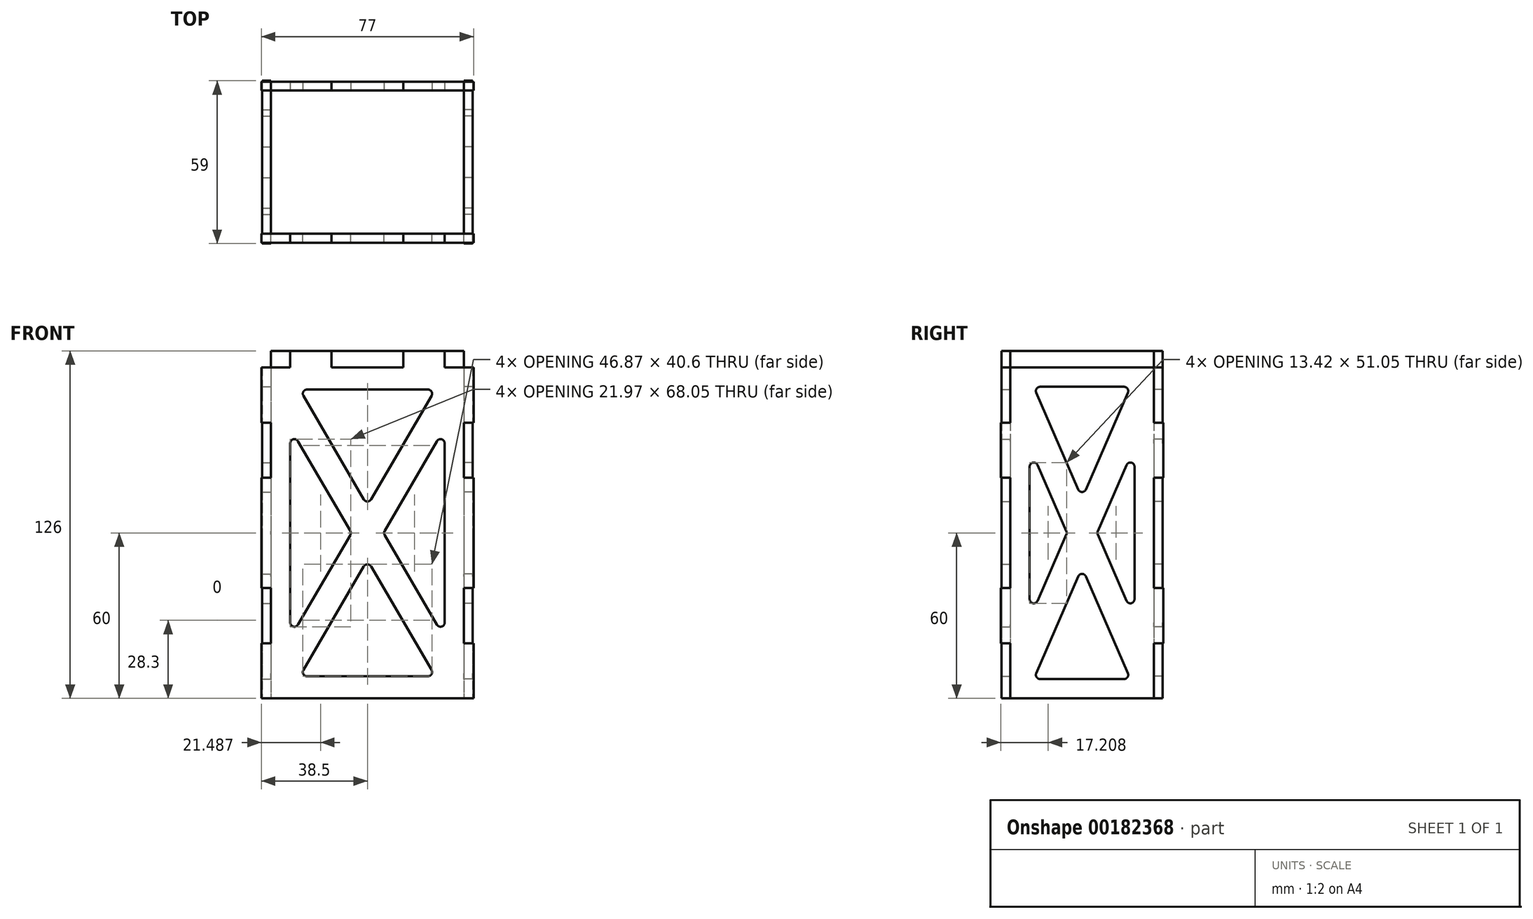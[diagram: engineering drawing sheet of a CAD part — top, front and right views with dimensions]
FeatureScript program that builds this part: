
annotation { "Feature Type Name" : "Feature", "Feature Type Description" : "" }
export const myFeature = defineFeature(function(context is Context, id is Id, definition is map)
    precondition{}
    {
        {
            var Q0;
            Q0=qCreatedBy(makeId("Top.planeOp"),FACE);
            var sketch = newSketch(context, id + "F0", { "sketchPlane" : qUnion([Q0])});
            skLineSegment(sketch, "E0.bottom", {"start": v(35, -26) * mm, "end": v(-35, -26) * mm});
            skLineSegment(sketch, "E0.top", {"start": v(35, 26) * mm, "end": v(-35, 26) * mm});
            skLineSegment(sketch, "E0.left", {"start": v(35, -26) * mm, "end": v(35, 26) * mm});
            skLineSegment(sketch, "E0.right", {"start": v(-35, -26) * mm, "end": v(-35, 26) * mm});
            skPoint(sketch, "E0.middle", {"position": v(0, 0) * mm});
            skSolve(sketch);
        }
        {
            var Q0;
            Q0 = qSketchRegion(id + "F0", true);
            extrude(context, id + "F1", {"entities" : qUnion([Q0]), "depth" : 126 * mm, "offsetDistance" : 25 * mm});
        }
        {
            var Q0;
            Q0=makeQuery(id+"F1.opExtrude","SWEPT_FACE",FACE,{"disambiguationData":[OSD([sQuery(id+"F0.wireOp",EDGE,"E0.bottom")])]});
            var sketch = newSketch(context, id + "F2", { "sketchPlane" : qUnion([Q0])});
            skLineSegment(sketch, "E1.0", {"start": v(28, 126) * mm, "end": v(13, 126) * mm});
            skLineSegment(sketch, "E2.0", {"start": v(38.5, 0) * mm, "end": v(-38.5, 0) * mm});
            skLineSegment(sketch, "E3.0", {"start": v(-38.5, 120) * mm, "end": v(-38.5, 100) * mm});
            skLineSegment(sketch, "E4.0", {"start": v(38.5, 120) * mm, "end": v(38.5, 100) * mm});
            skLineSegment(sketch, "E5.0", {"start": v(38.5, 120) * mm, "end": v(28, 120) * mm});
            skLineSegment(sketch, "E6.0", {"start": v(38.5, 100) * mm, "end": v(35, 100) * mm});
            skLineSegment(sketch, "E7.0", {"start": v(38.5, 80) * mm, "end": v(35, 80) * mm});
            skLineSegment(sketch, "E8.0", {"start": v(38.5, 20) * mm, "end": v(35, 20) * mm});
            skLineSegment(sketch, "E9.0", {"start": v(38.5, 40) * mm, "end": v(35, 40) * mm});
            skLineSegment(sketch, "E10.trimOffspring", {"start": v(-38.5, 80) * mm, "end": v(-38.5, 40) * mm});
            skLineSegment(sketch, "E11.trimOffspring", {"start": v(38.5, 80) * mm, "end": v(38.5, 40) * mm});
            skLineSegment(sketch, "E12.trimOffspring", {"start": v(35, 100) * mm, "end": v(35, 80) * mm});
            skLineSegment(sketch, "E13.trimOffspring", {"start": v(-28, 120) * mm, "end": v(-38.5, 120) * mm});
            skLineSegment(sketch, "E14.trimOffspring", {"start": v(-35, 100) * mm, "end": v(-35, 80) * mm});
            skLineSegment(sketch, "E15.trimOffspring", {"start": v(-35, 40) * mm, "end": v(-35, 20) * mm});
            skLineSegment(sketch, "E16.trimOffspring", {"start": v(38.5, 20) * mm, "end": v(38.5, 0) * mm});
            skLineSegment(sketch, "E17.trimOffspring", {"start": v(-38.5, 20) * mm, "end": v(-38.5, 0) * mm});
            skLineSegment(sketch, "E18.trimOffspring", {"start": v(35, 40) * mm, "end": v(35, 20) * mm});
            skLineSegment(sketch, "E19.trimOffspring", {"start": v(-35, 20) * mm, "end": v(-38.5, 20) * mm});
            skLineSegment(sketch, "E20.trimOffspring", {"start": v(-35, 40) * mm, "end": v(-38.5, 40) * mm});
            skLineSegment(sketch, "E21.trimOffspring", {"start": v(-35, 80) * mm, "end": v(-38.5, 80) * mm});
            skLineSegment(sketch, "E22.trimOffspring", {"start": v(-35, 100) * mm, "end": v(-38.5, 100) * mm});
            skPoint(sketch, "E23", {"position": v(0, 126) * mm});
            skLineSegment(sketch, "E24", {"start": v(-13, 126) * mm, "end": v(-13, 120) * mm});
            skLineSegment(sketch, "E25", {"start": v(-28, 126) * mm, "end": v(-28, 120) * mm});
            skLineSegment(sketch, "E26", {"start": v(13, 126) * mm, "end": v(13, 120) * mm});
            skLineSegment(sketch, "E27", {"start": v(28, 126) * mm, "end": v(28, 120) * mm});
            skPoint(sketch, "E28.0.start.orphan", {"position": v(-35, 126) * mm});
            skLineSegment(sketch, "E29.trimOffspring", {"start": v(-13, 126) * mm, "end": v(-28, 126) * mm});
            skPoint(sketch, "E30.0.start.orphan", {"position": v(35, 126) * mm});
            skLineSegment(sketch, "E31", {"start": v(-13, 120) * mm, "end": v(13, 120) * mm});
            skLineSegment(sketch, "E32", {"start": v(-35, 120) * mm, "end": v(35, 0) * mm, "construction": true});
            skLineSegment(sketch, "E33", {"start": v(35, 120) * mm, "end": v(-35, 0) * mm, "construction": true});
            skLineSegment(sketch, "E34", {"start": v(-28, 92.53) * mm, "end": v(-28, 27.47) * mm});
            skLineSegment(sketch, "E35", {"start": v(28, 92.53) * mm, "end": v(28, 27.47) * mm});
            skLineSegment(sketch, "E36", {"start": v(-21.93, 112) * mm, "end": v(21.93, 112) * mm});
            skLineSegment(sketch, "E37", {"start": v(-21.93, 8) * mm, "end": v(21.93, 8) * mm});
            skLineSegment(sketch, "E38.trimOffspring", {"start": v(-25.2, 93.28) * mm, "end": v(-6.23, 60.76) * mm});
            skLineSegment(sketch, "E39.trimOffspring", {"start": v(-23.23, 109.74) * mm, "end": v(-1.3, 72.14) * mm});
            skLineSegment(sketch, "E40.trimOffspring", {"start": v(25.2, 93.28) * mm, "end": v(6.23, 60.76) * mm});
            skLineSegment(sketch, "E41.trimOffspring", {"start": v(23.23, 109.74) * mm, "end": v(1.3, 72.14) * mm});
            skLineSegment(sketch, "E42.trimOffspring", {"start": v(6.23, 59.24) * mm, "end": v(25.2, 26.72) * mm});
            skLineSegment(sketch, "E43.trimOffspring", {"start": v(-6.23, 59.24) * mm, "end": v(-25.2, 26.72) * mm});
            skLineSegment(sketch, "E44.trimOffspring", {"start": v(-1.3, 47.86) * mm, "end": v(-23.23, 10.26) * mm});
            skLineSegment(sketch, "E45.trimOffspring", {"start": v(1.3, 47.86) * mm, "end": v(23.23, 10.26) * mm});
            skPoint(sketch, "E46.visualSharp", {"position": v(-28, 98.08) * mm});
            skArc(sketch, "E46.filletArc", {"start": v(-25.2, 93.28) * mm, "mid": v(-26.9, 93.98) * mm, "end": v(-28, 92.53) * mm});
            skPoint(sketch, "E47.visualSharp", {"position": v(-5.79, 60) * mm});
            skArc(sketch, "E47.filletArc", {"start": v(-6.23, 59.24) * mm, "mid": v(-6.03, 60) * mm, "end": v(-6.23, 60.76) * mm});
            skPoint(sketch, "E48.visualSharp", {"position": v(-28, 21.92) * mm});
            skArc(sketch, "E48.filletArc", {"start": v(-28, 27.47) * mm, "mid": v(-26.9, 26.02) * mm, "end": v(-25.2, 26.72) * mm});
            skPoint(sketch, "E49.visualSharp", {"position": v(-24.54, 8) * mm});
            skArc(sketch, "E49.filletArc", {"start": v(-23.23, 10.26) * mm, "mid": v(-23.23, 8.75) * mm, "end": v(-21.93, 8) * mm});
            skPoint(sketch, "E50.visualSharp", {"position": v(0, 50.08) * mm});
            skArc(sketch, "E50.filletArc", {"start": v(1.3, 47.86) * mm, "mid": v(0, 48.6) * mm, "end": v(-1.3, 47.86) * mm});
            skPoint(sketch, "E51.visualSharp", {"position": v(24.54, 8) * mm});
            skArc(sketch, "E51.filletArc", {"start": v(21.93, 8) * mm, "mid": v(23.23, 8.75) * mm, "end": v(23.23, 10.26) * mm});
            skPoint(sketch, "E52.visualSharp", {"position": v(5.79, 60) * mm});
            skArc(sketch, "E52.filletArc", {"start": v(6.23, 60.76) * mm, "mid": v(6.03, 60) * mm, "end": v(6.23, 59.24) * mm});
            skPoint(sketch, "E53.visualSharp", {"position": v(28, 21.92) * mm});
            skArc(sketch, "E53.filletArc", {"start": v(25.2, 26.72) * mm, "mid": v(26.9, 26.02) * mm, "end": v(28, 27.47) * mm});
            skPoint(sketch, "E54.visualSharp", {"position": v(28, 98.08) * mm});
            skArc(sketch, "E54.filletArc", {"start": v(28, 92.53) * mm, "mid": v(26.9, 93.98) * mm, "end": v(25.2, 93.28) * mm});
            skPoint(sketch, "E55.visualSharp", {"position": v(24.54, 112) * mm});
            skArc(sketch, "E55.filletArc", {"start": v(23.23, 109.74) * mm, "mid": v(23.23, 111.25) * mm, "end": v(21.93, 112) * mm});
            skPoint(sketch, "E56.visualSharp", {"position": v(-24.54, 112) * mm});
            skArc(sketch, "E56.filletArc", {"start": v(-21.93, 112) * mm, "mid": v(-23.23, 111.25) * mm, "end": v(-23.23, 109.74) * mm});
            skPoint(sketch, "E57.visualSharp", {"position": v(0, 69.92) * mm});
            skArc(sketch, "E57.filletArc", {"start": v(-1.3, 72.14) * mm, "mid": v(0, 71.4) * mm, "end": v(1.3, 72.14) * mm});
            skSolve(sketch);
        }
        {
            var Q0;
            Q0 = qSketchRegion(id + "F2", true);
            extrude(context, id + "F3", {"entities" : qUnion([Q0]), "depth" : 3.2 * mm, "offsetDistance" : 25 * mm});
        }
        {
            var Q0;
            Q0=makeQuery(id+"F1.opExtrude","SWEPT_FACE",FACE,{"disambiguationData":[OSD([sQuery(id+"F0.wireOp",EDGE,"E0.top")])]});
            var sketch = newSketch(context, id + "F4", { "sketchPlane" : qUnion([Q0])});
            skLineSegment(sketch, "E58.0.0", {"start": v(-38.5, 0) * mm, "end": v(-38.5, 20) * mm});
            skLineSegment(sketch, "E58.0.1", {"start": v(-38.5, 20) * mm, "end": v(-35, 20) * mm});
            skLineSegment(sketch, "E58.0.2", {"start": v(-35, 20) * mm, "end": v(-35, 40) * mm});
            skLineSegment(sketch, "E58.0.3", {"start": v(-35, 40) * mm, "end": v(-38.5, 40) * mm});
            skLineSegment(sketch, "E58.0.4", {"start": v(-38.5, 40) * mm, "end": v(-38.5, 80) * mm});
            skLineSegment(sketch, "E58.0.5", {"start": v(-38.5, 80) * mm, "end": v(-35, 80) * mm});
            skLineSegment(sketch, "E58.0.6", {"start": v(-35, 80) * mm, "end": v(-35, 100) * mm});
            skLineSegment(sketch, "E58.0.7", {"start": v(-35, 100) * mm, "end": v(-38.5, 100) * mm});
            skLineSegment(sketch, "E58.0.8", {"start": v(-38.5, 100) * mm, "end": v(-38.5, 120) * mm});
            skLineSegment(sketch, "E58.0.9", {"start": v(-38.5, 120) * mm, "end": v(-35, 120) * mm});
            skLineSegment(sketch, "E58.0.11", {"start": v(-35, 126) * mm, "end": v(-13, 126) * mm});
            skLineSegment(sketch, "E58.0.12", {"start": v(-13, 126) * mm, "end": v(-13, 120) * mm});
            skLineSegment(sketch, "E58.0.13", {"start": v(-13, 120) * mm, "end": v(13, 120) * mm});
            skLineSegment(sketch, "E58.0.14", {"start": v(13, 120) * mm, "end": v(13, 126) * mm});
            skLineSegment(sketch, "E58.0.15", {"start": v(13, 126) * mm, "end": v(35, 126) * mm});
            skLineSegment(sketch, "E58.0.17", {"start": v(35, 120) * mm, "end": v(38.5, 120) * mm});
            skLineSegment(sketch, "E58.0.18", {"start": v(38.5, 120) * mm, "end": v(38.5, 100) * mm});
            skLineSegment(sketch, "E58.0.19", {"start": v(38.5, 100) * mm, "end": v(35, 100) * mm});
            skLineSegment(sketch, "E58.0.20", {"start": v(35, 100) * mm, "end": v(35, 80) * mm});
            skLineSegment(sketch, "E58.0.21", {"start": v(35, 80) * mm, "end": v(38.5, 80) * mm});
            skLineSegment(sketch, "E58.0.22", {"start": v(38.5, 80) * mm, "end": v(38.5, 40) * mm});
            skLineSegment(sketch, "E58.0.23", {"start": v(38.5, 40) * mm, "end": v(35, 40) * mm});
            skLineSegment(sketch, "E58.0.24", {"start": v(35, 40) * mm, "end": v(35, 20) * mm});
            skLineSegment(sketch, "E58.0.25", {"start": v(35, 20) * mm, "end": v(38.5, 20) * mm});
            skLineSegment(sketch, "E58.0.26", {"start": v(38.5, 20) * mm, "end": v(38.5, 0) * mm});
            skLineSegment(sketch, "E58.0.27", {"start": v(38.5, 0) * mm, "end": v(-38.5, 0) * mm});
            skLineSegment(sketch, "E59.0", {"start": v(-23.23, 109.74) * mm, "end": v(-1.3, 72.14) * mm});
            skArc(sketch, "E60.0", {"start": v(-23.23, 109.74) * mm, "mid": v(-23.23, 111.25) * mm, "end": v(-21.93, 112) * mm});
            skLineSegment(sketch, "E61.0", {"start": v(21.93, 112) * mm, "end": v(-21.93, 112) * mm});
            skLineSegment(sketch, "E62.0", {"start": v(23.23, 109.74) * mm, "end": v(1.3, 72.14) * mm});
            skArc(sketch, "E63.0", {"start": v(21.93, 112) * mm, "mid": v(23.23, 111.25) * mm, "end": v(23.23, 109.74) * mm});
            skArc(sketch, "E64.0", {"start": v(1.3, 72.14) * mm, "mid": v(0, 71.4) * mm, "end": v(-1.3, 72.14) * mm});
            skLineSegment(sketch, "E65.0", {"start": v(-25.2, 93.28) * mm, "end": v(-6.23, 60.76) * mm});
            skArc(sketch, "E66.0", {"start": v(-28, 92.53) * mm, "mid": v(-26.9, 93.98) * mm, "end": v(-25.2, 93.28) * mm});
            skLineSegment(sketch, "E67.0", {"start": v(-28, 92.53) * mm, "end": v(-28, 27.47) * mm});
            skLineSegment(sketch, "E68.0", {"start": v(-6.23, 59.24) * mm, "end": v(-25.2, 26.72) * mm});
            skArc(sketch, "E69.0", {"start": v(-25.2, 26.72) * mm, "mid": v(-26.9, 26.02) * mm, "end": v(-28, 27.47) * mm});
            skArc(sketch, "E70.0", {"start": v(-6.23, 60.76) * mm, "mid": v(-6.03, 60) * mm, "end": v(-6.23, 59.24) * mm});
            skArc(sketch, "E71.0", {"start": v(6.23, 59.24) * mm, "mid": v(6.03, 60) * mm, "end": v(6.23, 60.76) * mm});
            skLineSegment(sketch, "E72.0", {"start": v(25.2, 93.28) * mm, "end": v(6.23, 60.76) * mm});
            skLineSegment(sketch, "E73.0", {"start": v(6.23, 59.24) * mm, "end": v(25.2, 26.72) * mm});
            skArc(sketch, "E74.0", {"start": v(25.2, 93.28) * mm, "mid": v(26.9, 93.98) * mm, "end": v(28, 92.53) * mm});
            skLineSegment(sketch, "E75.0", {"start": v(28, 92.53) * mm, "end": v(28, 27.47) * mm});
            skArc(sketch, "E76.0", {"start": v(28, 27.47) * mm, "mid": v(26.9, 26.02) * mm, "end": v(25.2, 26.72) * mm});
            skArc(sketch, "E77.0", {"start": v(-1.3, 47.86) * mm, "mid": v(0, 48.6) * mm, "end": v(1.3, 47.86) * mm});
            skLineSegment(sketch, "E78.0", {"start": v(1.3, 47.86) * mm, "end": v(23.23, 10.26) * mm});
            skLineSegment(sketch, "E79.0", {"start": v(-1.3, 47.86) * mm, "end": v(-23.23, 10.26) * mm});
            skArc(sketch, "E80.0", {"start": v(-21.93, 8) * mm, "mid": v(-23.23, 8.75) * mm, "end": v(-23.23, 10.26) * mm});
            skArc(sketch, "E81.0", {"start": v(23.23, 10.26) * mm, "mid": v(23.23, 8.75) * mm, "end": v(21.93, 8) * mm});
            skLineSegment(sketch, "E82.0", {"start": v(21.93, 8) * mm, "end": v(-21.93, 8) * mm});
            skLineSegment(sketch, "E83", {"start": v(-35, 120) * mm, "end": v(-35, 126) * mm});
            skLineSegment(sketch, "E84", {"start": v(35, 120) * mm, "end": v(35, 126) * mm});
            skPoint(sketch, "E85.orphan", {"position": v(28, 120) * mm});
            skPoint(sketch, "E86.orphan", {"position": v(-28, 120) * mm});
            skSolve(sketch);
        }
        {
            var Q0;
            Q0 = qSketchRegion(id + "F4", true);
            extrude(context, id + "F5", {"entities" : qUnion([Q0]), "depth" : 3.2 * mm, "offsetDistance" : 25 * mm});
        }
        {
            var Q0;
            Q0=makeQuery(id+"F1.opExtrude","SWEPT_FACE",FACE,{"disambiguationData":[OSD([sQuery(id+"F0.wireOp",EDGE,"E0.left")])]});
            var sketch = newSketch(context, id + "F6", { "sketchPlane" : qUnion([Q0])});
            skLineSegment(sketch, "E87.0", {"start": v(-26, 120) * mm, "end": v(-26, 100) * mm});
            skLineSegment(sketch, "E88.0", {"start": v(-29.5, 100) * mm, "end": v(-26, 100) * mm});
            skLineSegment(sketch, "E89.0", {"start": v(-29.5, 80) * mm, "end": v(-26, 80) * mm});
            skLineSegment(sketch, "E90.0", {"start": v(-26, 80) * mm, "end": v(-26, 40) * mm});
            skLineSegment(sketch, "E91.0", {"start": v(-29.5, 40) * mm, "end": v(-26, 40) * mm});
            skLineSegment(sketch, "E92.0", {"start": v(-29.5, 20) * mm, "end": v(-26, 20) * mm});
            skLineSegment(sketch, "E92.1", {"start": v(-26, 20) * mm, "end": v(-26, 0) * mm});
            skLineSegment(sketch, "E93.0", {"start": v(-26, 0) * mm, "end": v(26, 0) * mm});
            skLineSegment(sketch, "E94.0", {"start": v(26, 0) * mm, "end": v(26, 20) * mm});
            skLineSegment(sketch, "E95.0", {"start": v(29.5, 20) * mm, "end": v(26, 20) * mm});
            skLineSegment(sketch, "E96.0", {"start": v(29.5, 40) * mm, "end": v(26, 40) * mm});
            skLineSegment(sketch, "E97.0", {"start": v(26, 40) * mm, "end": v(26, 80) * mm});
            skLineSegment(sketch, "E98.0", {"start": v(29.5, 80) * mm, "end": v(26, 80) * mm});
            skLineSegment(sketch, "E99.0", {"start": v(29.5, 100) * mm, "end": v(26, 100) * mm});
            skLineSegment(sketch, "E100.0", {"start": v(26, 100) * mm, "end": v(26, 120) * mm});
            skLineSegment(sketch, "E101", {"start": v(-26, 120) * mm, "end": v(26, 120) * mm});
            skLineSegment(sketch, "E102.0", {"start": v(-26, 126) * mm, "end": v(-26, 0) * mm, "construction": true});
            skLineSegment(sketch, "E103.0", {"start": v(26, 126) * mm, "end": v(26, 0) * mm, "construction": true});
            skLineSegment(sketch, "E104.0", {"start": v(-29.5, 100) * mm, "end": v(-29.5, 80) * mm});
            skLineSegment(sketch, "E105.0", {"start": v(29.5, 100) * mm, "end": v(29.5, 80) * mm});
            skLineSegment(sketch, "E106.trimOffspring", {"start": v(29.5, 40) * mm, "end": v(29.5, 20) * mm});
            skLineSegment(sketch, "E107.trimOffspring", {"start": v(-29.5, 40) * mm, "end": v(-29.5, 20) * mm});
            skLineSegment(sketch, "E108", {"start": v(-26, 120) * mm, "end": v(26, 0) * mm, "construction": true});
            skLineSegment(sketch, "E109", {"start": v(26, 120) * mm, "end": v(-26, 0) * mm, "construction": true});
            skLineSegment(sketch, "E110", {"start": v(-15.23, 113) * mm, "end": v(15.23, 113) * mm});
            skLineSegment(sketch, "E111", {"start": v(-19, 84.04) * mm, "end": v(-19, 35.96) * mm});
            skLineSegment(sketch, "E112", {"start": v(19, 84.04) * mm, "end": v(19, 35.96) * mm});
            skLineSegment(sketch, "E113", {"start": v(-15.23, 7) * mm, "end": v(15.23, 7) * mm});
            skLineSegment(sketch, "E114.trimOffspring", {"start": v(5.7, 59.4) * mm, "end": v(16.12, 35.37) * mm});
            skLineSegment(sketch, "E115.trimOffspring", {"start": v(1.38, 44.25) * mm, "end": v(16.6, 9.1) * mm});
            skLineSegment(sketch, "E116.trimOffspring", {"start": v(-1.38, 44.25) * mm, "end": v(-16.6, 9.1) * mm});
            skLineSegment(sketch, "E117.trimOffspring", {"start": v(-5.7, 59.4) * mm, "end": v(-16.12, 35.37) * mm});
            skLineSegment(sketch, "E118.trimOffspring", {"start": v(-16.6, 110.9) * mm, "end": v(-1.38, 75.75) * mm});
            skLineSegment(sketch, "E119.trimOffspring", {"start": v(-16.12, 84.63) * mm, "end": v(-5.7, 60.6) * mm});
            skLineSegment(sketch, "E120.trimOffspring", {"start": v(16.6, 110.9) * mm, "end": v(1.38, 75.75) * mm});
            skLineSegment(sketch, "E121.trimOffspring", {"start": v(16.12, 84.63) * mm, "end": v(5.7, 60.6) * mm});
            skPoint(sketch, "E122.visualSharp", {"position": v(-17.52, 113) * mm});
            skArc(sketch, "E122.filletArc", {"start": v(-15.23, 113) * mm, "mid": v(-16.49, 112.32) * mm, "end": v(-16.6, 110.9) * mm});
            skPoint(sketch, "E123.visualSharp", {"position": v(17.52, 113) * mm});
            skArc(sketch, "E123.filletArc", {"start": v(16.6, 110.9) * mm, "mid": v(16.49, 112.32) * mm, "end": v(15.23, 113) * mm});
            skPoint(sketch, "E124.visualSharp", {"position": v(0, 72.58) * mm});
            skArc(sketch, "E124.filletArc", {"start": v(-1.38, 75.75) * mm, "mid": v(0, 74.85) * mm, "end": v(1.38, 75.75) * mm});
            skPoint(sketch, "E125.visualSharp", {"position": v(-19, 91.27) * mm});
            skArc(sketch, "E125.filletArc", {"start": v(-16.12, 84.63) * mm, "mid": v(-17.8, 85.5) * mm, "end": v(-19, 84.04) * mm});
            skPoint(sketch, "E126.visualSharp", {"position": v(-19, 28.73) * mm});
            skArc(sketch, "E126.filletArc", {"start": v(-19, 35.96) * mm, "mid": v(-17.8, 34.5) * mm, "end": v(-16.12, 35.37) * mm});
            skPoint(sketch, "E127.visualSharp", {"position": v(-5.45, 60) * mm});
            skArc(sketch, "E127.filletArc", {"start": v(-5.7, 59.4) * mm, "mid": v(-5.58, 60) * mm, "end": v(-5.7, 60.6) * mm});
            skPoint(sketch, "E128.visualSharp", {"position": v(19, 91.27) * mm});
            skArc(sketch, "E128.filletArc", {"start": v(19, 84.04) * mm, "mid": v(17.8, 85.5) * mm, "end": v(16.12, 84.63) * mm});
            skPoint(sketch, "E129.visualSharp", {"position": v(19, 28.73) * mm});
            skArc(sketch, "E129.filletArc", {"start": v(16.12, 35.37) * mm, "mid": v(17.8, 34.5) * mm, "end": v(19, 35.96) * mm});
            skPoint(sketch, "E130.visualSharp", {"position": v(5.45, 60) * mm});
            skArc(sketch, "E130.filletArc", {"start": v(5.7, 60.6) * mm, "mid": v(5.58, 60) * mm, "end": v(5.7, 59.4) * mm});
            skPoint(sketch, "E131.visualSharp", {"position": v(0, 47.42) * mm});
            skArc(sketch, "E131.filletArc", {"start": v(1.38, 44.25) * mm, "mid": v(0, 45.15) * mm, "end": v(-1.38, 44.25) * mm});
            skPoint(sketch, "E132.visualSharp", {"position": v(17.52, 7) * mm});
            skArc(sketch, "E132.filletArc", {"start": v(15.23, 7) * mm, "mid": v(16.49, 7.68) * mm, "end": v(16.6, 9.1) * mm});
            skPoint(sketch, "E133.visualSharp", {"position": v(-17.52, 7) * mm});
            skArc(sketch, "E133.filletArc", {"start": v(-16.6, 9.1) * mm, "mid": v(-16.49, 7.68) * mm, "end": v(-15.23, 7) * mm});
            skSolve(sketch);
        }
        {
            var Q0;
            Q0 = qSketchRegion(id + "F6", true);
            extrude(context, id + "F7", {"entities" : qUnion([Q0]), "depth" : 3.2 * mm, "offsetDistance" : 25 * mm});
        }
        {
            var Q0;
            Q0=makeQuery(id+"F1.opExtrude","SWEPT_FACE",FACE,{"disambiguationData":[OSD([sQuery(id+"F0.wireOp",EDGE,"E0.right")])]});
            var sketch = newSketch(context, id + "F8", { "sketchPlane" : qUnion([Q0])});
            skPoint(sketch, "E134.0", {"position": v(-26, 20) * mm});
            skPoint(sketch, "E134.1", {"position": v(-16.6, 110.9) * mm});
            skPoint(sketch, "E134.2", {"position": v(-5.7, 60.6) * mm});
            skPoint(sketch, "E134.4", {"position": v(26, 20) * mm});
            skPoint(sketch, "E134.5", {"position": v(26, 0) * mm});
            skLineSegment(sketch, "E134.6.0", {"start": v(-16.12, 84.63) * mm, "end": v(-5.7, 60.6) * mm});
            skArc(sketch, "E134.6.1", {"start": v(-5.7, 60.6) * mm, "mid": v(-5.58, 60) * mm, "end": v(-5.7, 59.4) * mm});
            skLineSegment(sketch, "E134.6.2", {"start": v(-5.7, 59.4) * mm, "end": v(-16.12, 35.37) * mm});
            skArc(sketch, "E134.6.3", {"start": v(-16.12, 35.37) * mm, "mid": v(-17.8, 34.5) * mm, "end": v(-19, 35.96) * mm});
            skLineSegment(sketch, "E134.6.4", {"start": v(-19, 35.96) * mm, "end": v(-19, 84.04) * mm});
            skArc(sketch, "E134.6.5", {"start": v(-19, 84.04) * mm, "mid": v(-17.8, 85.5) * mm, "end": v(-16.12, 84.63) * mm});
            skPoint(sketch, "E134.7", {"position": v(26, 100) * mm});
            skPoint(sketch, "E134.8", {"position": v(-19, 84.04) * mm});
            skLineSegment(sketch, "E134.9", {"start": v(-29.5, 80) * mm, "end": v(-26, 80) * mm});
            skPoint(sketch, "E134.10", {"position": v(19, 28.73) * mm});
            skPoint(sketch, "E134.11", {"position": v(26, 120) * mm});
            skLineSegment(sketch, "E134.12", {"start": v(-16.6, 110.9) * mm, "end": v(-1.38, 75.75) * mm});
            skLineSegment(sketch, "E134.13", {"start": v(26, 80) * mm, "end": v(26, 40) * mm});
            skPoint(sketch, "E134.14", {"position": v(-15.23, 113) * mm});
            skPoint(sketch, "E134.15", {"position": v(-29.5, 100) * mm});
            skPoint(sketch, "E134.16", {"position": v(0, 72.58) * mm});
            skLineSegment(sketch, "E134.17", {"start": v(5.7, 59.4) * mm, "end": v(16.12, 35.37) * mm});
            skPoint(sketch, "E134.18", {"position": v(-26, 120) * mm});
            skPoint(sketch, "E134.19", {"position": v(1.38, 75.75) * mm});
            skLineSegment(sketch, "E134.20", {"start": v(15.23, 7) * mm, "end": v(-15.23, 7) * mm});
            skPoint(sketch, "E134.21", {"position": v(-26, 40) * mm});
            skLineSegment(sketch, "E134.22.0", {"start": v(-16.6, 9.1) * mm, "end": v(-1.38, 44.25) * mm});
            skArc(sketch, "E134.22.1", {"start": v(-1.38, 44.25) * mm, "mid": v(0, 45.15) * mm, "end": v(1.38, 44.25) * mm});
            skLineSegment(sketch, "E134.22.2", {"start": v(1.38, 44.25) * mm, "end": v(16.6, 9.1) * mm});
            skArc(sketch, "E134.22.3", {"start": v(16.6, 9.1) * mm, "mid": v(16.49, 7.68) * mm, "end": v(15.23, 7) * mm});
            skLineSegment(sketch, "E134.22.4", {"start": v(15.23, 7) * mm, "end": v(-15.23, 7) * mm});
            skArc(sketch, "E134.22.5", {"start": v(-15.23, 7) * mm, "mid": v(-16.49, 7.68) * mm, "end": v(-16.6, 9.1) * mm});
            skPoint(sketch, "E134.23", {"position": v(29.5, 40) * mm});
            skPoint(sketch, "E134.24", {"position": v(-17.52, 7) * mm});
            skArc(sketch, "E134.25", {"start": v(16.6, 9.1) * mm, "mid": v(16.49, 7.68) * mm, "end": v(15.23, 7) * mm});
            skPoint(sketch, "E134.26", {"position": v(29.5, 80) * mm});
            skPoint(sketch, "E134.27", {"position": v(5.7, 59.4) * mm});
            skPoint(sketch, "E134.29", {"position": v(16.12, 35.37) * mm});
            skArc(sketch, "E134.30", {"start": v(-16.12, 35.37) * mm, "mid": v(-17.8, 34.5) * mm, "end": v(-19, 35.96) * mm});
            skPoint(sketch, "E134.31", {"position": v(-29.5, 100) * mm});
            skPoint(sketch, "E134.32", {"position": v(-1.38, 44.25) * mm});
            skPoint(sketch, "E134.33", {"position": v(16.12, 84.63) * mm});
            skPoint(sketch, "E134.34", {"position": v(-26, 80) * mm});
            skPoint(sketch, "E134.35", {"position": v(15.23, 111.5) * mm});
            skPoint(sketch, "E134.36", {"position": v(15.23, 7) * mm});
            skLineSegment(sketch, "E134.37.0", {"start": v(29.5, 100) * mm, "end": v(29.5, 80) * mm});
            skPoint(sketch, "E134.38", {"position": v(-16.6, 110.9) * mm});
            skPoint(sketch, "E134.39", {"position": v(26, 80) * mm});
            skPoint(sketch, "E134.40", {"position": v(16.6, 9.1) * mm});
            skPoint(sketch, "E134.42", {"position": v(-26, 20) * mm});
            skPoint(sketch, "E134.43", {"position": v(-29.5, 80) * mm});
            skPoint(sketch, "E134.44", {"position": v(-7.08, 60) * mm});
            skPoint(sketch, "E134.46", {"position": v(-16.12, 84.63) * mm});
            skPoint(sketch, "E134.47", {"position": v(-1.38, 44.25) * mm});
            skPoint(sketch, "E134.49", {"position": v(0, 0) * mm});
            skArc(sketch, "E134.50", {"start": v(19, 35.96) * mm, "mid": v(17.8, 34.5) * mm, "end": v(16.12, 35.37) * mm});
            skPoint(sketch, "E134.51", {"position": v(-26, 0) * mm});
            skPoint(sketch, "E134.52", {"position": v(-19, 28.73) * mm});
            skPoint(sketch, "E134.53", {"position": v(-15.23, 7) * mm});
            skPoint(sketch, "E134.54", {"position": v(-16.12, 35.37) * mm});
            skPoint(sketch, "E134.55", {"position": v(5.45, 60) * mm});
            skLineSegment(sketch, "E134.56.0", {"start": v(29.5, 40) * mm, "end": v(29.5, 20) * mm});
            skLineSegment(sketch, "E134.56.1", {"start": v(29.5, 20) * mm, "end": v(26, 20) * mm});
            skLineSegment(sketch, "E134.56.3", {"start": v(26, 40) * mm, "end": v(29.5, 40) * mm});
            skArc(sketch, "E134.57", {"start": v(15.23, 113) * mm, "mid": v(16.49, 112.32) * mm, "end": v(16.6, 110.9) * mm});
            skPoint(sketch, "E134.58", {"position": v(26, 80) * mm});
            skPoint(sketch, "E134.59", {"position": v(19, 35.96) * mm});
            skPoint(sketch, "E134.60", {"position": v(-5.7, 60.6) * mm});
            skLineSegment(sketch, "E134.61", {"start": v(26, 20) * mm, "end": v(26, 0) * mm});
            skPoint(sketch, "E134.62", {"position": v(-26, 100) * mm});
            skPoint(sketch, "E134.63", {"position": v(19, 91.27) * mm});
            skPoint(sketch, "E134.64", {"position": v(-26, 0) * mm});
            skPoint(sketch, "E134.65", {"position": v(26, 0) * mm});
            skPoint(sketch, "E134.66", {"position": v(5.7, 60.6) * mm});
            skPoint(sketch, "E134.67", {"position": v(-19, 35.96) * mm});
            skLineSegment(sketch, "E134.68", {"start": v(-29.5, 100) * mm, "end": v(-26, 100) * mm});
            skPoint(sketch, "E134.70", {"position": v(26, 120) * mm});
            skPoint(sketch, "E134.71", {"position": v(17.52, 7) * mm});
            skPoint(sketch, "E134.72", {"position": v(26, 126) * mm});
            skPoint(sketch, "E134.73", {"position": v(5.7, 60.6) * mm});
            skPoint(sketch, "E134.74", {"position": v(17.5, 84.04) * mm});
            skPoint(sketch, "E134.75", {"position": v(-26, 120) * mm});
            skLineSegment(sketch, "E134.76", {"start": v(16.12, 84.63) * mm, "end": v(5.7, 60.6) * mm});
            skPoint(sketch, "E134.77", {"position": v(1.38, 44.25) * mm});
            skPoint(sketch, "E134.78", {"position": v(15.23, 113) * mm});
            skPoint(sketch, "E134.79", {"position": v(26, 120) * mm});
            skPoint(sketch, "E134.80", {"position": v(26, 0) * mm});
            skPoint(sketch, "E134.81", {"position": v(-26, 80) * mm});
            skPoint(sketch, "E134.82", {"position": v(-15.23, 111.5) * mm});
            skLineSegment(sketch, "E134.83", {"start": v(1.38, 44.25) * mm, "end": v(16.6, 9.1) * mm});
            skPoint(sketch, "E134.84", {"position": v(15.23, 8.5) * mm});
            skPoint(sketch, "E134.85", {"position": v(-26, 0) * mm});
            skPoint(sketch, "E134.87", {"position": v(1.38, 75.75) * mm});
            skPoint(sketch, "E134.88", {"position": v(16.6, 110.9) * mm});
            skLineSegment(sketch, "E134.89", {"start": v(-19, 84.04) * mm, "end": v(-19, 35.96) * mm});
            skPoint(sketch, "E134.90", {"position": v(-26, 40) * mm});
            skPoint(sketch, "E134.91", {"position": v(-29.5, 20) * mm});
            skPoint(sketch, "E134.92", {"position": v(0, 43.65) * mm});
            skArc(sketch, "E134.93", {"start": v(-15.23, 7) * mm, "mid": v(-16.49, 7.68) * mm, "end": v(-16.6, 9.1) * mm});
            skPoint(sketch, "E134.94", {"position": v(16.6, 9.1) * mm});
            skPoint(sketch, "E134.95", {"position": v(-15.23, 7) * mm});
            skPoint(sketch, "E134.96", {"position": v(19, 35.96) * mm});
            skLineSegment(sketch, "E134.97", {"start": v(26, 120) * mm, "end": v(-26, 0) * mm, "construction": true});
            skArc(sketch, "E134.98", {"start": v(-19, 84.04) * mm, "mid": v(-17.8, 85.5) * mm, "end": v(-16.12, 84.63) * mm});
            skPoint(sketch, "E134.99", {"position": v(29.5, 80) * mm});
            skPoint(sketch, "E134.100", {"position": v(-26, 0) * mm});
            skLineSegment(sketch, "E134.101.0", {"start": v(-29.5, 20) * mm, "end": v(-29.5, 40) * mm});
            skLineSegment(sketch, "E134.101.3", {"start": v(-26, 20) * mm, "end": v(-29.5, 20) * mm});
            skPoint(sketch, "E134.102", {"position": v(-16.12, 35.37) * mm});
            skPoint(sketch, "E134.103", {"position": v(26, 40) * mm});
            skPoint(sketch, "E134.104", {"position": v(-1.38, 75.75) * mm});
            skPoint(sketch, "E134.105", {"position": v(-19, 91.27) * mm});
            skLineSegment(sketch, "E134.106", {"start": v(26, 120) * mm, "end": v(-26, 120) * mm});
            skPoint(sketch, "E134.107", {"position": v(17.52, 113) * mm});
            skLineSegment(sketch, "E134.108", {"start": v(26, 0) * mm, "end": v(-26, 0) * mm});
            skArc(sketch, "E134.109", {"start": v(1.38, 75.75) * mm, "mid": v(0, 74.85) * mm, "end": v(-1.38, 75.75) * mm});
            skPoint(sketch, "E134.110", {"position": v(-19, 35.96) * mm});
            skPoint(sketch, "E134.111", {"position": v(16.6, 110.9) * mm});
            skPoint(sketch, "E134.112", {"position": v(-16.6, 9.1) * mm});
            skLineSegment(sketch, "E134.113", {"start": v(-26, 120) * mm, "end": v(26, 0) * mm, "construction": true});
            skPoint(sketch, "E134.114", {"position": v(-29.5, 20) * mm});
            skPoint(sketch, "E134.115", {"position": v(-5.45, 60) * mm});
            skPoint(sketch, "E134.116", {"position": v(-1.38, 75.75) * mm});
            skPoint(sketch, "E134.117", {"position": v(-5.7, 59.4) * mm});
            skLineSegment(sketch, "E134.118.0", {"start": v(-29.5, 80) * mm, "end": v(-29.5, 100) * mm});
            skPoint(sketch, "E134.120", {"position": v(29.5, 40) * mm});
            skArc(sketch, "E134.121", {"start": v(16.12, 84.63) * mm, "mid": v(17.8, 85.5) * mm, "end": v(19, 84.04) * mm});
            skPoint(sketch, "E134.122", {"position": v(-26, 126) * mm});
            skPoint(sketch, "E134.123", {"position": v(-17.5, 84.04) * mm});
            skLineSegment(sketch, "E134.124", {"start": v(-26, 0) * mm, "end": v(-26, 20) * mm});
            skPoint(sketch, "E134.125", {"position": v(-16.12, 84.63) * mm});
            skPoint(sketch, "E134.126", {"position": v(17.5, 35.96) * mm});
            skPoint(sketch, "E134.127", {"position": v(-26, 120) * mm});
            skLineSegment(sketch, "E134.128", {"start": v(-16.12, 84.63) * mm, "end": v(-5.7, 60.6) * mm});
            skPoint(sketch, "E134.129", {"position": v(19, 84.04) * mm});
            skPoint(sketch, "E134.130", {"position": v(-26, 100) * mm});
            skPoint(sketch, "E134.131", {"position": v(0, 76.35) * mm});
            skPoint(sketch, "E134.132", {"position": v(26, 0) * mm});
            skLineSegment(sketch, "E134.133.1", {"start": v(26, 120) * mm, "end": v(-26, 120) * mm});
            skPoint(sketch, "E134.134", {"position": v(26, 40) * mm});
            skPoint(sketch, "E134.135", {"position": v(16.12, 84.63) * mm});
            skLineSegment(sketch, "E134.136", {"start": v(-5.7, 59.4) * mm, "end": v(-16.12, 35.37) * mm});
            skPoint(sketch, "E134.138", {"position": v(29.5, 20) * mm});
            skPoint(sketch, "E134.139", {"position": v(-15.23, 8.5) * mm});
            skPoint(sketch, "E134.141", {"position": v(16.12, 35.37) * mm});
            skLineSegment(sketch, "E134.142", {"start": v(26, 120) * mm, "end": v(26, 100) * mm});
            skPoint(sketch, "E134.143", {"position": v(5.7, 59.4) * mm});
            skArc(sketch, "E134.144", {"start": v(-5.7, 60.6) * mm, "mid": v(-5.58, 60) * mm, "end": v(-5.7, 59.4) * mm});
            skPoint(sketch, "E134.146", {"position": v(-16.6, 9.1) * mm});
            skPoint(sketch, "E134.147", {"position": v(19, 84.04) * mm});
            skLineSegment(sketch, "E134.148.9", {"start": v(-26, 40) * mm, "end": v(-26, 80) * mm});
            skLineSegment(sketch, "E134.148.11", {"start": v(-26, 100) * mm, "end": v(-26, 120) * mm});
            skPoint(sketch, "E134.149", {"position": v(-17.52, 113) * mm});
            skLineSegment(sketch, "E134.150", {"start": v(-1.38, 44.25) * mm, "end": v(-16.6, 9.1) * mm});
            skPoint(sketch, "E134.151", {"position": v(29.5, 20) * mm});
            skPoint(sketch, "E134.152", {"position": v(-29.5, 80) * mm});
            skLineSegment(sketch, "E134.153.0", {"start": v(16.6, 110.9) * mm, "end": v(1.38, 75.75) * mm});
            skArc(sketch, "E134.153.1", {"start": v(1.38, 75.75) * mm, "mid": v(0, 74.85) * mm, "end": v(-1.38, 75.75) * mm});
            skLineSegment(sketch, "E134.153.2", {"start": v(-1.38, 75.75) * mm, "end": v(-16.6, 110.9) * mm});
            skArc(sketch, "E134.153.3", {"start": v(-16.6, 110.9) * mm, "mid": v(-16.49, 112.32) * mm, "end": v(-15.23, 113) * mm});
            skLineSegment(sketch, "E134.153.4", {"start": v(-15.23, 113) * mm, "end": v(15.23, 113) * mm});
            skArc(sketch, "E134.153.5", {"start": v(15.23, 113) * mm, "mid": v(16.49, 112.32) * mm, "end": v(16.6, 110.9) * mm});
            skPoint(sketch, "E134.154", {"position": v(-15.23, 113) * mm});
            skPoint(sketch, "E134.155", {"position": v(26, 100) * mm});
            skLineSegment(sketch, "E134.156", {"start": v(-29.5, 40) * mm, "end": v(-26, 40) * mm});
            skPoint(sketch, "E134.157", {"position": v(15.23, 7) * mm});
            skLineSegment(sketch, "E134.158", {"start": v(19, 84.04) * mm, "end": v(19, 35.96) * mm});
            skPoint(sketch, "E134.159", {"position": v(-29.5, 40) * mm});
            skPoint(sketch, "E134.160", {"position": v(-29.5, 40) * mm});
            skPoint(sketch, "E134.161", {"position": v(0, 47.42) * mm});
            skLineSegment(sketch, "E134.162", {"start": v(29.5, 100) * mm, "end": v(26, 100) * mm});
            skArc(sketch, "E134.163", {"start": v(-1.38, 44.25) * mm, "mid": v(0, 45.15) * mm, "end": v(1.38, 44.25) * mm});
            skPoint(sketch, "E134.164", {"position": v(1.38, 44.25) * mm});
            skPoint(sketch, "E134.166", {"position": v(-17.5, 35.96) * mm});
            skArc(sketch, "E134.167", {"start": v(5.7, 59.4) * mm, "mid": v(5.58, 60) * mm, "end": v(5.7, 60.6) * mm});
            skPoint(sketch, "E134.168", {"position": v(29.5, 100) * mm});
            skPoint(sketch, "E134.169", {"position": v(-5.7, 59.4) * mm});
            skPoint(sketch, "E134.170", {"position": v(26, 20) * mm});
            skLineSegment(sketch, "E134.171.0", {"start": v(16.12, 35.37) * mm, "end": v(5.7, 59.4) * mm});
            skArc(sketch, "E134.171.1", {"start": v(5.7, 59.4) * mm, "mid": v(5.58, 60) * mm, "end": v(5.7, 60.6) * mm});
            skLineSegment(sketch, "E134.171.2", {"start": v(5.7, 60.6) * mm, "end": v(16.12, 84.63) * mm});
            skArc(sketch, "E134.171.3", {"start": v(16.12, 84.63) * mm, "mid": v(17.8, 85.5) * mm, "end": v(19, 84.04) * mm});
            skLineSegment(sketch, "E134.171.4", {"start": v(19, 84.04) * mm, "end": v(19, 35.96) * mm});
            skArc(sketch, "E134.171.5", {"start": v(19, 35.96) * mm, "mid": v(17.8, 34.5) * mm, "end": v(16.12, 35.37) * mm});
            skPoint(sketch, "E134.172", {"position": v(7.08, 60) * mm});
            skPoint(sketch, "E134.173", {"position": v(29.5, 100) * mm});
            skArc(sketch, "E134.174", {"start": v(-16.6, 110.9) * mm, "mid": v(-16.49, 112.32) * mm, "end": v(-15.23, 113) * mm});
            skPoint(sketch, "E134.176", {"position": v(-19, 84.04) * mm});
            skPoint(sketch, "E134.177", {"position": v(15.23, 113) * mm});
            skLineSegment(sketch, "E134.178", {"start": v(29.5, 80) * mm, "end": v(26, 80) * mm});
            skSolve(sketch);
        }
        {
            var Q0;
            Q0 = qSketchRegion(id + "F8", true);
            extrude(context, id + "F9", {"entities" : qUnion([Q0]), "depth" : 3.2 * mm, "offsetDistance" : 25 * mm});
        }
    });
